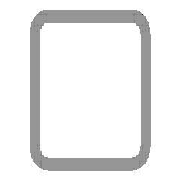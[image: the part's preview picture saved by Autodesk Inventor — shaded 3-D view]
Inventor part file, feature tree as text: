
AUTODESK INVENTOR PART (.ipt)
format: ipt  version: 2022 (Build 260153000, 153)  size: 131,584 bytes
history: native  units: mm (DEFAULTED — no unit token found)
features: other x4, sketch x3, plane x1
ambient origin geometry x8: Origin, YZ Plane, XZ Plane, XY Plane, X Axis, Y Axis, Z Axis, Center Point
bodies: Solid1 (feature_tree), Body (feature_tree)
feature tree (8):
  parser-record x1  (decoder bookkeeping rows leaked as tree rows — omitted from the tree; the rows remain in map.json)
  other  "Driven Length"
  other  "Start Plane"
  other  "End Plane"
  sketch  "Sketch"  dims[d7=4.0mm d9=40.0mm d11=40.0mm d12=2.0mm d13=-0.0mm d14=300.0mm d15=20.0mm d16=20.0mm d17=90.0deg d18=300.0mm]
  sketch  "Sketch3"  dims[d3=300.0mm]
  plane  "Work Plane3"
  sketch  "Sketch4"  dims[d4=0.0mm]
